# Revit family: IS_Moments_K7058_BIM_GB
name_source: partatom
category: Plumbing Fixtures
revit_build: Autodesk Revit MEP 2014 (Build: 20130308_1515(x64)
units: mm (PartAtom-declared; Revit-internal decimal feet)

## types (1)
- K705801 - Moments Slow clousing  Seat & Cover
    Accessories = www.idealspec.co.uk
    AreaUnits = millimeters
    Assembly Code = C1030200
    AssetType = Fixed
    BIMObjectName = ISI_IdealStandard_WCSeatsAndCovers_Moments_K7058
    BarCode = 4015413978453
    Brand = Ideal Standard
    CWFU = 0
    ConnectionType = Plumbing
    Cost = 0 $
    Default Elevation = 0 mm  [stored 0 ft]
    Description = Moments seat and cover, slow closing
    DurationUnit = year
    ECA = No
    ExpectedLife = 15
    Features = Moments seat and cover, slow closing
    Finish = White
    HWFU = 0
    Help = www.idealspec.co.uk/contact-us.html
    IfcExportAs = IfcSanitaryTerminalType
    IfcExportType = WCSEAT
    InstallationInstructions = www.idealspec.co.uk/resources.html
    LinearUnits = millimeters
    ManufacturerURL = www.idealspec.co.uk
    Model = K705801
    ModelNumber = K705801
    ModelReference = Moments seat and cover, slow closing
    NBSDescription = WC seats and covers
    NBSReference = 45-35-70/391
    Name = WCSeatsAndCovers_Moments_K7058_IdealStandard
    NettWeight = 3 Kg
    NominalDepth = 478 mm  [stored 1.56824 ft]
    NominalHeight = 55 mm
    NominalLength = 0 mm  [stored 0 ft]
    NominalWidth = 358 mm
    PanColor = White
    PanMaterial = Vitreous china
    PanMounting = BackToWall
    ProductInformation = www.idealspec.co.uk/assets/datasheet/K705801
    Shape = Sculptured
    Size = 478 x 55 x 359 mm
    Space = Internal
    SpilloverLevel = 0 mm  [stored 0 ft]
    ToiletPanType = WashDown
    ToiletType = Other
    URL = www.idealspec.co.uk
    Uniclass2015Code = Pr_40_20_93_95
    Uniclass2015Title = WC seats and covers
    Uniclass2015Version = Products v1.1
    Version = 1
    VolumeUnits = Litres
    WFU = 0
    WarrantyDescription = Manufacturers Warranty
    WarrantyDurationParts = 99
    WarrantyDurationUnit = year

note: [stored X ft] marks values corroborated as IEEE doubles in the binary element streams (Revit-internal decimal feet)

## geometry (parser evidence)
native form markers: Sweep x6
no freeform markers — native parametric forms only
